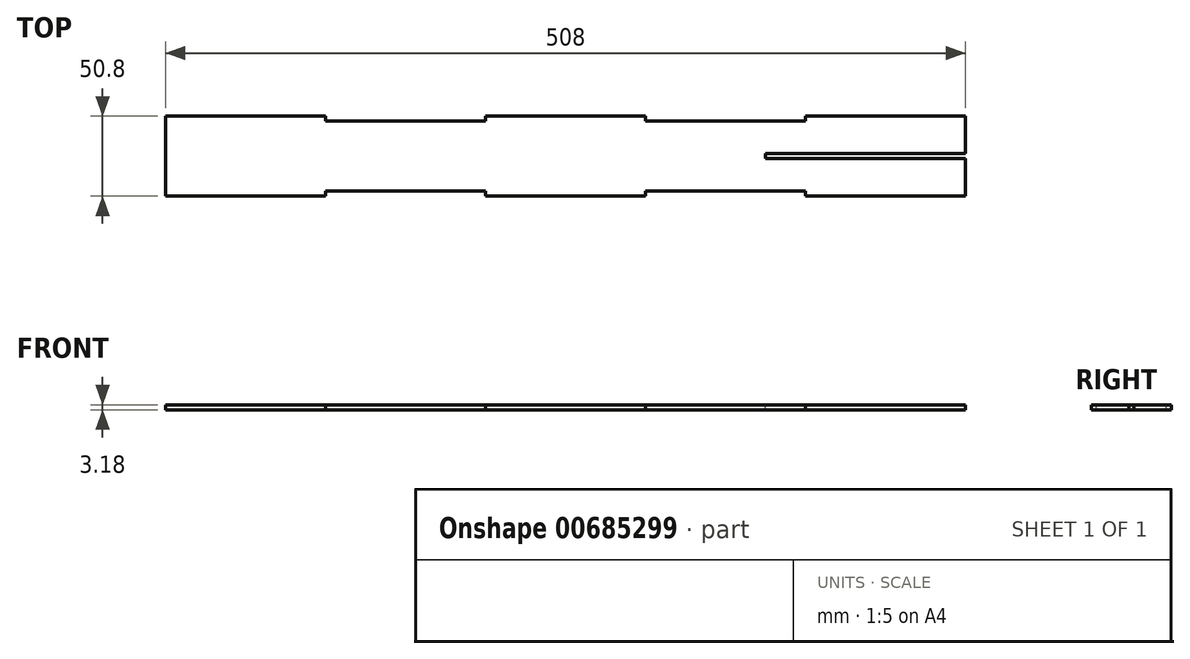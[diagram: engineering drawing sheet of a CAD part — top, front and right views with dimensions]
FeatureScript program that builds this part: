
annotation { "Feature Type Name" : "Feature", "Feature Type Description" : "" }
export const myFeature = defineFeature(function(context is Context, id is Id, definition is map)
    precondition{}
    {
        {
            var Q0;
            Q0=qCreatedBy(makeId("Top.planeOp"),FACE);
            var sketch = newSketch(context, id + "F0", { "sketchPlane" : qUnion([Q0])});
            skLineSegment(sketch, "E0.bottom", {"start": v(0, 0) * mm, "end": v(508, 0) * mm});
            skLineSegment(sketch, "E0.top", {"start": v(0, 50.8) * mm, "end": v(508, 50.8) * mm});
            skLineSegment(sketch, "E0.left", {"start": v(0, 0) * mm, "end": v(0, 50.8) * mm});
            skLineSegment(sketch, "E0.right", {"start": v(508, 0) * mm, "end": v(508, 50.8) * mm});
            skSolve(sketch);
        }
        {
            var Q0;
            Q0 = qSketchRegion(id + "F0", true);
            var Q1;
            Q1=makeQuery(id+"F0.imprint","IMPRINT",FACE,{"disambiguationData":[TD([[makeQuery(id+"F0.imprint","IMPRINT",EDGE,{"derivedFrom":sQuery(id+"F0.wireOp",EDGE,"E0.bottom")}),1.0]])]});
            extrude(context, id + "F1", {"entities" : qUnion([Q0, Q1]), "depth" : 3.17 * mm, "offsetDistance" : 25.4 * mm});
        }
        {
            var Q0;
            Q0=makeQuery(id+"F1.opExtrude","CAP_FACE",FACE,{"disambiguationData":[OSD([sQuery(id+"F0.wireOp",EDGE,"E0.bottom"),sQuery(id+"F0.wireOp",EDGE,"E0.top"),sQuery(id+"F0.wireOp",EDGE,"E0.left"),sQuery(id+"F0.wireOp",EDGE,"E0.right")])],"isStart":false});
            var sketch = newSketch(context, id + "F2", { "sketchPlane" : qUnion([Q0])});
            skLineSegment(sketch, "E1.bottom", {"start": v(101.6, 0) * mm, "end": v(203.2, 0) * mm});
            skLineSegment(sketch, "E1.top", {"start": v(101.6, 3.18) * mm, "end": v(203.2, 3.18) * mm});
            skLineSegment(sketch, "E1.left", {"start": v(101.6, 0) * mm, "end": v(101.6, 3.18) * mm});
            skLineSegment(sketch, "E1.right", {"start": v(203.2, 0) * mm, "end": v(203.2, 3.18) * mm});
            skLineSegment(sketch, "E2.bottom", {"start": v(304.8, 0) * mm, "end": v(406.4, 0) * mm});
            skLineSegment(sketch, "E2.top", {"start": v(304.8, 3.18) * mm, "end": v(406.4, 3.18) * mm});
            skLineSegment(sketch, "E2.left", {"start": v(304.8, 0) * mm, "end": v(304.8, 3.18) * mm});
            skLineSegment(sketch, "E2.right", {"start": v(406.4, 0) * mm, "end": v(406.4, 3.18) * mm});
            skSolve(sketch);
        }
        {
            var Q0;
            Q0 = qSketchRegion(id + "F2", true);
            extrude(context, id + "F3", {"entities" : qUnion([Q0]), "operationType" : NewBodyOperationType.REMOVE, "oppositeDirection" : true, "depth" : 25.4 * mm, "offsetDistance" : 25.4 * mm});
        }
        {
            var Q0;
            Q0=makeQuery(id+"F1.opExtrude","CAP_FACE",FACE,{"disambiguationData":[OSD([sQuery(id+"F0.wireOp",EDGE,"E0.bottom"),sQuery(id+"F0.wireOp",EDGE,"E0.top"),sQuery(id+"F0.wireOp",EDGE,"E0.left"),sQuery(id+"F0.wireOp",EDGE,"E0.right")])],"isStart":false});
            var sketch = newSketch(context, id + "F4", { "sketchPlane" : qUnion([Q0])});
            skLineSegment(sketch, "E3.bottom", {"start": v(101.6, 50.8) * mm, "end": v(203.2, 50.8) * mm});
            skLineSegment(sketch, "E3.top", {"start": v(101.6, 47.63) * mm, "end": v(203.2, 47.63) * mm});
            skLineSegment(sketch, "E3.left", {"start": v(101.6, 50.8) * mm, "end": v(101.6, 47.63) * mm});
            skLineSegment(sketch, "E3.right", {"start": v(203.2, 50.8) * mm, "end": v(203.2, 47.63) * mm});
            skLineSegment(sketch, "E4.bottom", {"start": v(304.8, 50.8) * mm, "end": v(406.4, 50.8) * mm});
            skLineSegment(sketch, "E4.top", {"start": v(304.8, 47.63) * mm, "end": v(406.4, 47.63) * mm});
            skLineSegment(sketch, "E4.left", {"start": v(304.8, 50.8) * mm, "end": v(304.8, 47.63) * mm});
            skLineSegment(sketch, "E4.right", {"start": v(406.4, 50.8) * mm, "end": v(406.4, 47.63) * mm});
            skSolve(sketch);
        }
        {
            var Q0;
            Q0 = qSketchRegion(id + "F4", true);
            extrude(context, id + "F5", {"entities" : qUnion([Q0]), "operationType" : NewBodyOperationType.REMOVE, "oppositeDirection" : true, "depth" : 25.4 * mm, "offsetDistance" : 25.4 * mm});
        }
        {
            var Q0;
            Q0=makeQuery(id+"F1.opExtrude","CAP_FACE",FACE,{"disambiguationData":[OSD([sQuery(id+"F0.wireOp",EDGE,"E0.bottom"),sQuery(id+"F0.wireOp",EDGE,"E0.top"),sQuery(id+"F0.wireOp",EDGE,"E0.left"),sQuery(id+"F0.wireOp",EDGE,"E0.right")])],"isStart":false});
            var sketch = newSketch(context, id + "F6", { "sketchPlane" : qUnion([Q0])});
            skLineSegment(sketch, "E5.bottom", {"start": v(508, 23.81) * mm, "end": v(381, 23.81) * mm});
            skLineSegment(sketch, "E5.top", {"start": v(508, 26.99) * mm, "end": v(381, 26.99) * mm});
            skLineSegment(sketch, "E5.left", {"start": v(508, 23.81) * mm, "end": v(508, 26.99) * mm});
            skLineSegment(sketch, "E5.right", {"start": v(381, 23.81) * mm, "end": v(381, 26.99) * mm});
            skSolve(sketch);
        }
        {
            var Q0;
            Q0 = qSketchRegion(id + "F6", true);
            extrude(context, id + "F7", {"entities" : qUnion([Q0]), "operationType" : NewBodyOperationType.REMOVE, "oppositeDirection" : true, "depth" : 25.4 * mm, "offsetDistance" : 25.4 * mm});
        }
    });
